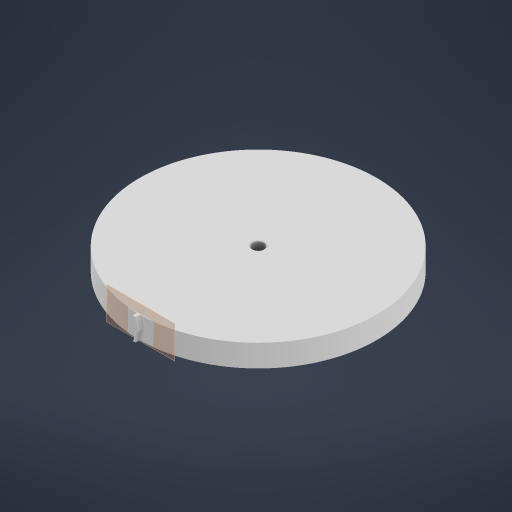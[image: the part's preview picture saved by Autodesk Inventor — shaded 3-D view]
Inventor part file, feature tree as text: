
AUTODESK INVENTOR PART (.ipt)
format: ipt  version: 2023 (Build 270158030, 158C)  size: 215,040 bytes
history: native  units: in
note: dims shown in document units (in); Inventor stores cm internally (conversion verified against a paired STEP export)
features: extrude x3, sketch x3, plane x1, fillet x1
ambient origin geometry x8: Origin, YZ Plane, XZ Plane, XY Plane, X Axis, Y Axis, Z Axis, Center Point
bodies: Solid1 (feature_tree)
feature tree (8):
  extrude  "Extrusion1"  Depth=0.5906in TaperAngle=0.0deg
  plane  "Work Plane1"
  extrude  "Extrusion2"  Depth=3.1299in
  extrude  "Extrusion8"  Depth=0.0394in
  fillet  "Fillet2"  Radius=0.1378in
  sketch  "Sketch3"  dims[d0=6.2992in d1=0.5906in d2=0.0in]
  sketch  "Sketch8"  dims[d3=3.1299in d4=0.0787in]
  sketch  "Sketch20"  dims[d5=0.0787in d6=0.0787in d7=0.1378in d8=0.0in d40=0.0394in d46=0.3071in d47=0.5906in d48=0.0in d41=0.0in d42=0.0in d43=0.0in]
